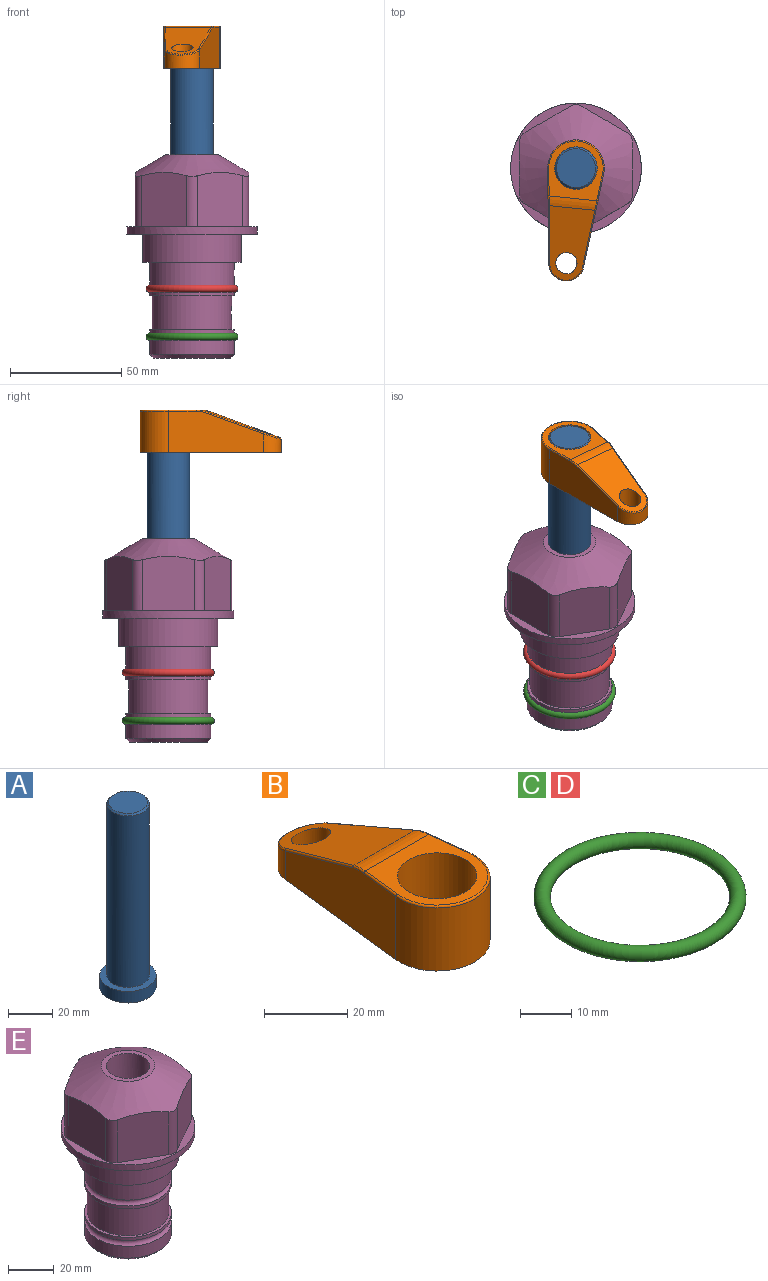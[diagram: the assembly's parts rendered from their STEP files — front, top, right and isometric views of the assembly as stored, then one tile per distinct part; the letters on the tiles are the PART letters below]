
ASSEMBLY  parts=5 mates=3
PART A: 6 faces, bbox 25.4x25.4x101.6 mm
  f0: plane 17.46x17.46mm, normal (0,0,1), area 239.5mm2, adj f5
  f1: plane 25.4x25.4mm, normal (0,0,-1), area 506.7mm2, adj f2
  f2: cylinder r=12.7mm len=25.4mm, axis (0,0,1), area 506.7mm2, adj f1,f3
  f3: plane 25.4x25.4mm, normal (0,0,1), area 221.7mm2, adj f2,f4
  f4: cylinder r=9.53mm len=94.46mm, axis (0,0,1), area 5653mm2, adj f3,f5
  f5: cone r=8.73mm half-angle=45deg, axis (0,0,-1), area 64.4mm2, adj f0,f4
PART B: 44 faces, bbox 27.5x64.5x19.1 mm
  f0: plane 2.3x0.95mm, normal (0,0,-1), area 1mm2, adj f25,f30,f34
  f1: plane 63.5x25.4mm, normal (0,0,-1), area 561.7mm2, adj f2,f3,f4,f5,f6,f7,f19,f20
  f2: cylinder r=12.7mm len=25.4mm, axis (0,0,-1), area 792.2mm2, adj f1,f3,f5,f13
  f3: plane 42.33x18.54mm, normal (0.99,0.11,0), area 647mm2, adj f1,f2,f4,f11,f12,f14
  f4: cylinder r=7.94mm len=15.78mm, axis (0,0,-1), area 158.6mm2, adj f1,f3,f5,f16
  f5: plane 42.33x18.54mm, normal (-0.99,0.11,0), area 647mm2, adj f1,f2,f4,f15,f17,f18
  f6: cylinder r=9.53mm len=19.05mm, axis (0,0,-1), area 1140.1mm2, adj f1,f8
  f7: cylinder r=4.76mm len=10.98mm, axis (0,0,-1), area 276.1mm2, adj f1,f9
  f8: plane 25.83x24.38mm, normal (0,0,1), area 262.2mm2, adj f6,f10,f11,f13,f15
  f9: plane 32.49x20.55mm, normal (0,0.34,0.94), area 489.9mm2, adj f7,f10,f14,f16,f18
  f10: cylinder r=12.7mm len=21.49mm, axis (-1,0,0), area 93.2mm2, adj f8,f9,f12,f17
  f11: cylinder r=0.51mm len=12.34mm, axis (0.11,-0.99,0), area 9.9mm2, adj f3,f8,f12,f13
  f12: bspline ~7.62x1.64mm, area 3.5mm2, adj f3,f10,f11,f14
  f13: torus R=12.19mm, axis (0,0,1), area 33.6mm2, adj f2,f8,f11,f15
  f14: cylinder r=0.51mm len=26.01mm, axis (0.1,-0.93,0.34), area 21.6mm2, adj f3,f9,f12,f16
  f15: cylinder r=0.51mm len=12.34mm, axis (0.11,0.99,0), area 9.9mm2, adj f5,f8,f13,f17
  f16: bspline ~15.78x7.05mm, area 15.7mm2, adj f4,f9,f14,f18
  f17: bspline ~7.62x1.64mm, area 3.5mm2, adj f5,f10,f15,f18
  f18: cylinder r=0.51mm len=26.01mm, axis (0.1,0.93,-0.34), area 21.6mm2, adj f5,f9,f16,f17
  f19: plane 21.6x14.29mm, normal (-0.99,-0.11,0), area 242.6mm2, adj f1,f26,f28,f34,f36,f38
  f20: plane 21.6x14.29mm, normal (0.99,-0.11,0), area 242.6mm2, adj f1,f27,f29,f37,f39,f41
  f21: cylinder r=12.7mm len=14.29mm, axis (0,0,-1), area 173.2mm2, adj f1,f26,f27,f30,f31,f33
  f22: cylinder r=7.94mm len=7.63mm, axis (0,0,-1), area 53.8mm2, adj f1,f28,f29,f42
  f23: plane 2.3x0.95mm, normal (0,0,-1), area 1mm2, adj f25,f33,f37
  f24: plane 17.94x12.32mm, normal (0,-0.34,-0.94), area 191.2mm2, adj f25,f38,f41,f42
  f25: cylinder r=9.53mm len=12.93mm, axis (-1,0,0), area 37.5mm2, adj f0,f23,f24,f31,f36,f39
  f26: cylinder r=1.59mm len=14.29mm, axis (0,0,-1), area 49mm2, adj f1,f19,f21,f32
  f27: cylinder r=1.59mm len=14.29mm, axis (0,0,-1), area 49mm2, adj f1,f20,f21,f35
  f28: cylinder r=1.59mm len=7.28mm, axis (0,0,-1), area 22.1mm2, adj f1,f19,f22,f40
  f29: cylinder r=1.59mm len=7.28mm, axis (0,0,-1), area 22.1mm2, adj f1,f20,f22,f43
  f30: torus R=14.29mm, axis (0,0,1), area 5.8mm2, adj f0,f21,f31,f32
  f31: bspline ~11.06x2.73mm, area 20.8mm2, adj f21,f25,f30,f33
  f32: sphere r=1.59mm, area 5.4mm2, adj f26,f30,f34
  f33: torus R=14.29mm, axis (0,0,1), area 5.8mm2, adj f21,f23,f31,f35
  f34: cylinder r=1.59mm len=1.68mm, axis (-0.11,0.99,0), area 2.4mm2, adj f0,f19,f32,f36
  f35: sphere r=1.59mm, area 5.4mm2, adj f27,f33,f37
  f36: bspline ~5.82x2.33mm, area 7.7mm2, adj f19,f25,f34,f38
  f37: cylinder r=1.59mm len=1.68mm, axis (0.11,0.99,0), area 2.4mm2, adj f20,f23,f35,f39
  f38: cylinder r=1.59mm len=18.33mm, axis (0.1,-0.93,0.34), area 46.7mm2, adj f19,f24,f36,f40
  f39: bspline ~5.82x2.33mm, area 7.7mm2, adj f20,f25,f37,f41
  f40: sphere r=1.59mm, area 3.6mm2, adj f28,f38,f42
  f41: cylinder r=1.59mm len=18.33mm, axis (0.1,0.93,-0.34), area 46.7mm2, adj f20,f24,f39,f43
  f42: bspline ~8.31x1.84mm, area 15.3mm2, adj f22,f24,f40,f43
  f43: sphere r=1.59mm, area 3.6mm2, adj f29,f41,f42
PART C: 1 faces, bbox 44.7x44.7x3.2 mm
  f0: torus R=19.05mm, axis (0,0,1), area 1193.9mm2
PART D: same geometry as C
PART E: 36 faces, bbox 58.7x58.7x91.2 mm
  f0: cylinder r=17.78mm len=35.56mm, axis (0,0,1), area 1670.8mm2, adj f23,f24,f31
  f1: cylinder r=19.05mm len=38.1mm, axis (0,0,1), area 1191.9mm2, adj f26,f27,f30
  f2: plane 58.66x58.66mm, normal (0,0,-1), area 1150.6mm2, adj f3,f28
  f3: cylinder r=29.33mm len=58.66mm, axis (0,0,-1), area 585.1mm2, adj f2,f4
  f4: plane 58.66x58.66mm, normal (0,0,1), area 475.9mm2, adj f3,f5,f6,f7,f8,f9,f10,f11
  f5: plane 24.5x20.32mm, normal (0.5,-0.87,0), area 562.8mm2, adj f4,f15,f16,f17
  f6: plane 24.5x20.32mm, normal (-0.5,-0.87,0), area 562.8mm2, adj f4,f14,f15,f17
  f7: plane 24.5x23.48mm, normal (-1,0,0), area 562.8mm2, adj f4,f13,f14,f17
  f8: plane 24.5x20.32mm, normal (-0.5,0.87,0), area 562.8mm2, adj f4,f12,f13,f17
  f9: plane 24.5x20.32mm, normal (0.5,0.87,0), area 562.8mm2, adj f4,f11,f12,f17
  f10: plane 24.5x23.48mm, normal (1,0,0), area 562.8mm2, adj f4,f11,f16,f17
  f11: cylinder r=5.08mm len=23.01mm, axis (0,0,-1), area 121.2mm2, adj f4,f9,f10,f17
  f12: cylinder r=5.08mm len=23.01mm, axis (0,0,-1), area 121.2mm2, adj f4,f8,f9,f17
  f13: cylinder r=5.08mm len=23.01mm, axis (0,0,-1), area 121.2mm2, adj f4,f7,f8,f17
  f14: cylinder r=5.08mm len=23.01mm, axis (0,0,-1), area 121.2mm2, adj f4,f6,f7,f17
  f15: cylinder r=5.08mm len=23.01mm, axis (0,0,-1), area 121.2mm2, adj f4,f5,f6,f17
  f16: cylinder r=5.08mm len=23.01mm, axis (0,0,-1), area 121.2mm2, adj f4,f5,f10,f17
  f17: cone r=11.73mm half-angle=60deg, axis (0,0,-1), area 2071.8mm2, adj f5,f6,f7,f8,f9,f10,f11,f12
  f18: plane 23.46x23.46mm, normal (0,0,1), area 147.4mm2, adj f17,f35
  f19: plane 34.93x34.93mm, normal (0,0,-1), area 958mm2, adj f29
  f20: cylinder r=19.05mm len=38.1mm, axis (0,0,1), area 760.1mm2, adj f21,f29
  f21: torus R=19.05mm, axis (0,0,1), area 565.3mm2, adj f20,f22
  f22: cylinder r=19.05mm len=38.1mm, axis (0,0,1), area 190mm2, adj f21,f23
  f23: plane 38.1x38.1mm, normal (0,0,1), area 146.9mm2, adj f0,f22
  f24: plane 38.1x38.1mm, normal (0,0,-1), area 146.9mm2, adj f0,f25
  f25: cylinder r=19.05mm len=38.1mm, axis (0,0,1), area 190mm2, adj f24,f26
  f26: torus R=19.05mm, axis (0,0,1), area 565.3mm2, adj f1,f25
  f27: plane 44.45x44.45mm, normal (0,0,-1), area 411.7mm2, adj f1,f28
  f28: cylinder r=22.23mm len=44.45mm, axis (0,0,1), area 1773.5mm2, adj f2,f27
  f29: cone r=19.05mm half-angle=45deg, axis (0,0,1), area 257.5mm2, adj f19,f20
  f30: cylinder r=3.17mm len=6.75mm, axis (-1,0,0), area 128mm2, adj f1,f33
  f31: cylinder r=3.17mm len=6.35mm, axis (-1,0,0), area 102.5mm2, adj f0,f33
  f32: plane 25.4x25.4mm, normal (0,0,1), area 506.7mm2, adj f33
  f33: cylinder r=12.7mm len=66.42mm, axis (0,0,-1), area 5236.2mm2, adj f30,f31,f32,f34
  f34: cone r=9.53mm half-angle=30deg, axis (0,0,-1), area 443.4mm2, adj f33,f35
  f35: cylinder r=9.53mm len=19.05mm, axis (0,0,-1), area 849mm2, adj f18,f34
PLACE A rot(axis=(0,0,-1),95.8deg) t=(0,0,19.69)mm
PLACE B rot(axis=(0,0,1),174.2deg) t=(0,0,74.3)mm
PLACE C t=(0,0,-21.59)mm
PLACE D at identity
PLACE E at identity fixed
MATE fastened C.f0 <-> E.f0  axis (0,0,1) through (0,0,-46.1)mm
MATE cylindrical A.f2 <-> E.f0  axis (0,0,1) through (0,0,45.32)mm
MATE fastened B.f2 <-> A.f2  axis (0,0,1) through (0,0,93.35)mm
